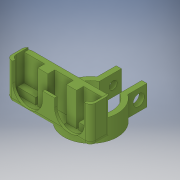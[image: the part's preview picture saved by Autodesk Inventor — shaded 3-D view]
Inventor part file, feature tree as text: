
AUTODESK INVENTOR PART (.ipt)
format: ipt  version: 2018 (Build 220112000, 112)  size: 324,608 bytes
history: native  units: in
note: dims shown in document units (in); Inventor stores cm internally (conversion verified against a paired STEP export)
features: extrude x8, sketch x8, fillet x4, reference x3, other x2, projected_geometry x1
ambient origin geometry x8: Origin, YZ Plane, XZ Plane, XY Plane, X Axis, Y Axis, Z Axis, Center Point
bodies: Solid1 (feature_tree)
feature tree (26):
  extrude  "Extrusion1"  Depth=0.125in
  extrude  "Extrusion2"  Depth=0.125in
  extrude  "Extrusion3"  Depth=0.125in
  extrude  "Extrusion4"  Depth=0.25in
  extrude  "Extrusion5"  Depth=0.194in
  extrude  "Extrusion7"  Depth=0.04in
  extrude  "Extrusion8"  Depth=0.8125in TaperAngle=0.0deg
  extrude  "Extrusion9"  Depth=0.125in
  fillet  "Fillet1"  Radius=0.05in
  fillet  "Fillet2"  Radius=0.05in
  fillet  "Fillet3"  Radius=0.05in
  fillet  "Fillet4"  Radius=0.05in
  sketch  "Sketch1"  dims[d0=1.05in d1=0.125in]
  sketch  "Sketch2"  dims[d2=0.125in d3=0.375in]
  sketch  "Sketch3"  dims[d4=1.0in d5=0.125in]
  sketch  "Sketch4"  dims[d6=0.5in d7=0.0in d8=0.25in]
  sketch  "Sketch5"  dims[d9=0.2in d10=0.194in]
  sketch  "Sketch7"  dims[d11=1.0in d12=0.0in d13=0.04in]
  projected_geometry  "Projected Loop3"
  sketch  "Sketch8"  dims[d14=1.0in d15=0.0in d18=0.8125in d19=0.0in]
  sketch  "Sketch9"  dims[d20=1.95in d21=0.975in d22=0.05in d23=0.05in d24=0.05in d25=0.05in d26=0.445in d27=0.0in d28=0.9125in d29=0.8in d30=0.05in d31=0.05in d35=0.17in d36=0.0in d37=0.25in d38=0.25in d39=0.5in d40=0.5in d41=0.17in d42=0.0in d43=0.05in d44=0.05in d45=0.0625in d46=0.0in d47=0.05in d48=0.125in d49=0.125in d50=0.25in d51=0.125in]
  reference  "Reference1"
  reference  "Reference2"
  reference  "Reference3"
  other  "Assembly1"
  other  "Ultrasonic_sensor:1"
